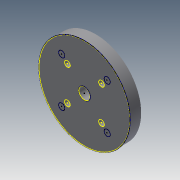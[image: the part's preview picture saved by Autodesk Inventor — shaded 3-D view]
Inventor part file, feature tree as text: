
AUTODESK INVENTOR PART (.ipt)
format: ipt  version: 2015 (Build 190159000, 159)  size: 103,424 bytes
history: native  units: mm
features: other x5, sketch x3, extrude x1, projected_geometry x1
ambient origin geometry x8: Origin, YZ Plane, XZ Plane, XY Plane, X Axis, Y Axis, Z Axis, Center Point
bodies: Body1 (feature_tree)
feature tree (10):
  other  "Blocks"
  extrude  "Extrusion3"  Depth=10.0mm
  sketch  "Sketch4"  dims[d6=5.0mm]
  sketch  "Sketch5"  dims[d7=15.0mm d8=15.0mm d9=10.0mm d10=0.0mm]
  sketch  "Sketch1"  dims[d0=80.0mm d3=10.0mm]
  other  "Block1"
  projected_geometry  "Projected Loop2"
  other  "Block2"
  other  "Block2:1"
  other  "Block2:2"
